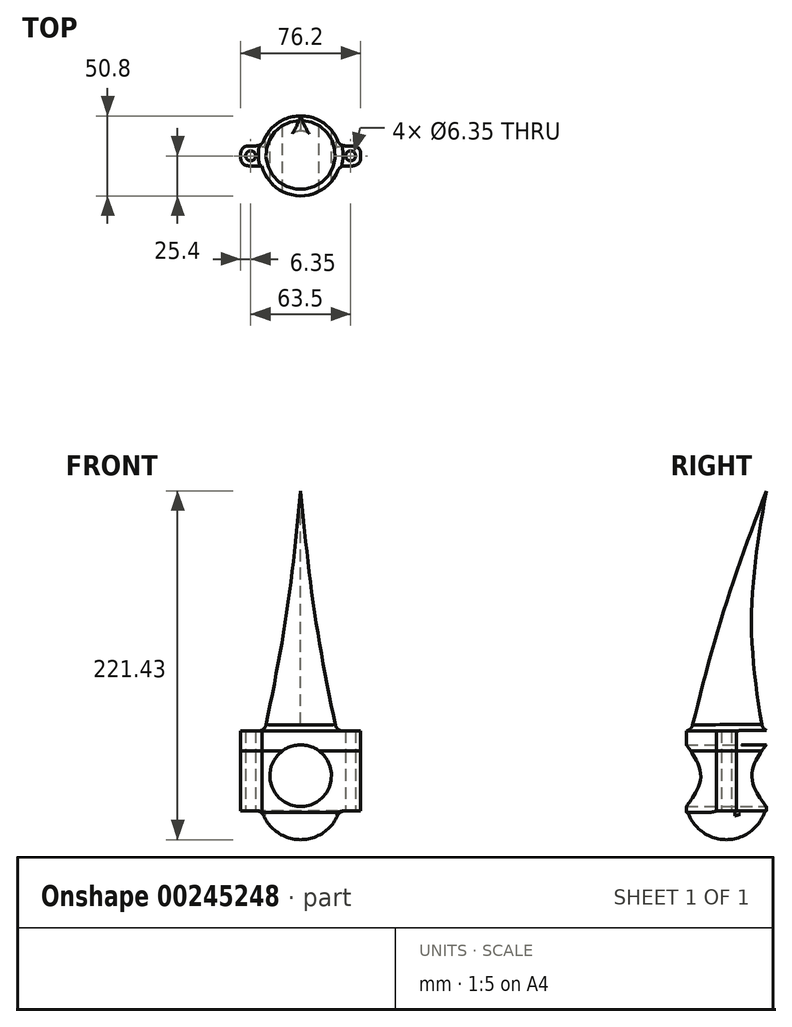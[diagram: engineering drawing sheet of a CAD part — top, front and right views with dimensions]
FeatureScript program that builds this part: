
annotation { "Feature Type Name" : "Feature", "Feature Type Description" : "" }
export const myFeature = defineFeature(function(context is Context, id is Id, definition is map)
    precondition{}
    {
        {
            var Q0;
            Q0=qCreatedBy(makeId("Right.planeOp"),FACE);
            var sketch = newSketch(context, id + "F0", { "sketchPlane" : qUnion([Q0])});
            skPoint(sketch, "E0", {"position": v(25.4, 165.1) * mm});
            skFitSpline(sketch, "E1", {"points": [v(0, 0) * mm, v(25.4, 165.1) * mm], "startDerivative": vector(11.53, 261.51) * mm, "endDerivative": vector(41.6, 123.81) * mm});
            skPoint(sketch, "E2", {"position": v(2.05, 36.75) * mm});
            skPoint(sketch, "E3", {"position": v(4.31, 63.88) * mm});
            skPoint(sketch, "E4", {"position": v(7.85, 92.76) * mm});
            skPoint(sketch, "E5", {"position": v(10.88, 110.73) * mm});
            skSolve(sketch);
        }
        {
            var Q0;
            Q0=qCreatedBy(makeId("Top.planeOp"),FACE);
            var sketch = newSketch(context, id + "F1", { "sketchPlane" : qUnion([Q0])});
            skCircle(sketch, "E6", {"center": v(0, 0) * mm, "radius": 25.4 * mm});
            skSolve(sketch);
        }
        {
            var Q0;
            Q0=sQuery(id+"F0.wireOp",EDGE,"E1");
            cPoint(context, id + "F2", {"entities" : qUnion([Q0]), "parameter" : 0.5});
        }
        {
            var Q0;
            Q0=sQuery(id+"F0.wireOp",EDGE,"E1");
            var Q1;
            Q1 = qCreatedBy(id + "F2" ,VERTEX);
            cPlane(context, id + "F3", {"entities" : qUnion([Q0, Q1]), "cplaneType" : CPlaneType.CURVE_POINT, "offset" : 25.4 * mm, "width" : 152.4 * mm, "height" : 152.4 * mm});
        }
        {
            var Q0;
            Q0=qCreatedBy(id+"F3.planeOp",FACE);
            var sketch = newSketch(context, id + "F4", { "sketchPlane" : qUnion([Q0])});
            skCircle(sketch, "E7", {"center": v(0, -4.31) * mm, "radius": 9.53 * mm});
            skSolve(sketch);
        }
        {
            var Q0;
            Q0=sQuery(id+"F0.wireOp",VERTEX,"E2");
            var Q1;
            Q1=sQuery(id+"F0.wireOp",EDGE,"E1");
            cPlane(context, id + "F5", {"entities" : qUnion([Q0, Q1]), "cplaneType" : CPlaneType.CURVE_POINT, "offset" : 25.4 * mm, "width" : 152.4 * mm, "height" : 152.4 * mm});
        }
        {
            var Q0;
            Q0=sQuery(id+"F0.wireOp",VERTEX,"E3");
            var Q1;
            Q1=sQuery(id+"F0.wireOp",EDGE,"E1");
            cPlane(context, id + "F6", {"entities" : qUnion([Q0, Q1]), "cplaneType" : CPlaneType.CURVE_POINT, "offset" : 25.4 * mm, "width" : 152.4 * mm, "height" : 152.4 * mm});
        }
        {
            var Q0;
            Q0=makeQuery(id+"F1.imprint","IMPRINT",FACE,{"disambiguationData":[TD([[makeQuery(id+"F1.imprint","IMPRINT",EDGE,{"derivedFrom":sQuery(id+"F1.wireOp",EDGE,"E6")}),1.0]])]});
            var Q1;
            Q1 = qSketchRegion(id + "F4", true);
            var Q2;
            Q2=sQuery(id+"F0.wireOp",VERTEX,"E0");
            loft(context, id + "F7", {"sheetProfilesArray" : [{ "sheetProfileEntities" : qUnion([Q0]) }, { "sheetProfileEntities" : qUnion([Q1]) }, { "sheetProfileEntities" : qUnion([Q2]) }]});
        }
        {
            var Q0;
            Q0=qCreatedBy(makeId("Top.planeOp"),FACE);
            var sketch = newSketch(context, id + "F8", { "sketchPlane" : qUnion([Q0])});
            skArc(sketch, "E8", {"start": v(24.6, 6.35) * mm, "mid": v(0, 25.4) * mm, "end": v(-24.6, 6.35) * mm});
            skLineSegment(sketch, "E9.bottom", {"start": v(-38.1, 6.35) * mm, "end": v(-24.6, 6.35) * mm});
            skLineSegment(sketch, "E9.top", {"start": v(-38.1, -6.35) * mm, "end": v(-24.6, -6.35) * mm});
            skLineSegment(sketch, "E9.left", {"start": v(-38.1, 6.35) * mm, "end": v(-38.1, -6.35) * mm});
            skLineSegment(sketch, "E9.right", {"start": v(38.1, 6.35) * mm, "end": v(38.1, -6.35) * mm});
            skLineSegment(sketch, "E10.trimOffspring", {"start": v(24.6, -6.35) * mm, "end": v(38.1, -6.35) * mm});
            skLineSegment(sketch, "E11.trimOffspring", {"start": v(24.6, 6.35) * mm, "end": v(38.1, 6.35) * mm});
            skArc(sketch, "E12.trimOffspring", {"start": v(-24.6, -6.35) * mm, "mid": v(0, -25.4) * mm, "end": v(24.6, -6.35) * mm});
            skPoint(sketch, "E13", {"position": v(-31.75, 0) * mm});
            skPoint(sketch, "E14", {"position": v(31.75, 0) * mm});
            skSolve(sketch);
        }
        {
            var Q0;
            Q0 = qSketchRegion(id + "F8", true);
            extrude(context, id + "F9", {"entities" : qUnion([Q0]), "operationType" : NewBodyOperationType.ADD, "depth" : 12.7 * mm});
        }
        {
            var Q0;
            Q0 = qSketchRegion(id + "F8", true);
            extrude(context, id + "F10", {"entities" : qUnion([Q0]), "oppositeDirection" : true, "depth" : 38.1 * mm});
        }
        {
            var Q0;
            Q0=qCreatedBy(makeId("Front.planeOp"),FACE);
            var sketch = newSketch(context, id + "F11", { "sketchPlane" : qUnion([Q0])});
            skCircle(sketch, "E15", {"center": v(0, -15.71) * mm, "radius": 19.57 * mm});
            skSolve(sketch);
        }
        {
            var Q0;
            Q0 = qSketchRegion(id + "F11", true);
            extrude(context, id + "F12", {"entities" : qUnion([Q0]), "operationType" : NewBodyOperationType.REMOVE, "depth" : 25.4 * mm, "hasSecondDirection" : true, "secondDirectionOppositeDirection" : true, "secondDirectionDepth" : 25.4 * mm});
        }
        {
            var Q0;
            Q0=makeQuery(id+"F9.boolean.opBoolean","INTERSECT",EDGE,{"derivedFrom":[makeQuery(id+"F7.opLoft","SWEPT_FACE",FACE,{"disambiguationData":[OSD([sQuery(id+"F0.wireOp",VERTEX,"E0"),sQuery(id+"F1.wireOp",EDGE,"E6"),sQuery(id+"F4.wireOp",EDGE,"E7")])]}),makeQuery(id+"F9.opExtrude","CAP_FACE",FACE,{"disambiguationData":[OSD([sQuery(id+"F8.wireOp",EDGE,"E8"),sQuery(id+"F8.wireOp",EDGE,"E9.bottom"),sQuery(id+"F8.wireOp",EDGE,"E9.top"),sQuery(id+"F8.wireOp",EDGE,"E9.left"),sQuery(id+"F8.wireOp",EDGE,"E9.right"),sQuery(id+"F8.wireOp",EDGE,"E10.trimOffspring"),sQuery(id+"F8.wireOp",EDGE,"E11.trimOffspring"),sQuery(id+"F8.wireOp",EDGE,"E12.trimOffspring")])],"isStart":false})]});
            fillet(context, id + "F13", {"entities" : qUnion([Q0]), "radius" : 5.08 * mm, "tangentPropagation" : true, "allowEdgeOverflow" : false});
        }
        {
            var Q0;
            Q0=qCreatedBy(makeId("Front.planeOp"),FACE);
            var sketch = newSketch(context, id + "F14", { "sketchPlane" : qUnion([Q0])});
            skArc(sketch, "E16", {"start": v(0, -56.33) * mm, "mid": v(15.32, -51.25) * mm, "end": v(24.6, -38.03) * mm});
            skLineSegment(sketch, "E17", {"start": v(24.6, -38.03) * mm, "end": v(0, -38.07) * mm});
            skLineSegment(sketch, "E18", {"start": v(0, -64.16) * mm, "end": v(0, -21.9) * mm, "construction": true});
            skLineSegment(sketch, "E19", {"start": v(0, -56.33) * mm, "end": v(0, -38.07) * mm});
            skSolve(sketch);
        }
        {
            var Q0;
            Q0 = qSketchRegion(id + "F14", true);
            var Q1;
            Q1=sQuery(id+"F14.wireOp",EDGE,"E18");
            revolve(context, id + "F15", {"operationType" : NewBodyOperationType.ADD, "entities" : qUnion([Q0]), "axis" : qUnion([Q1]), "revolveType" : RevolveType.FULL});
        }
        {
            var Q0;
            Q0=makeQuery(id+"F10.opExtrude","CAP_FACE",FACE,{"disambiguationData":[OSD([sQuery(id+"F8.wireOp",EDGE,"E8"),sQuery(id+"F8.wireOp",EDGE,"E9.bottom"),sQuery(id+"F8.wireOp",EDGE,"E9.top"),sQuery(id+"F8.wireOp",EDGE,"E9.left"),sQuery(id+"F8.wireOp",EDGE,"E9.right"),sQuery(id+"F8.wireOp",EDGE,"E10.trimOffspring"),sQuery(id+"F8.wireOp",EDGE,"E11.trimOffspring"),sQuery(id+"F8.wireOp",EDGE,"E12.trimOffspring")])],"isStart":false});
            var sketch = newSketch(context, id + "F16", { "sketchPlane" : qUnion([Q0])});
            skPoint(sketch, "E20", {"position": v(31.75, 0) * mm});
            skPoint(sketch, "E20.positionSnap0", {"position": v(38.1, 0) * mm});
            skPoint(sketch, "E21", {"position": v(-31.75, 0) * mm});
            skSolve(sketch);
        }
        {
            var Q0;
            Q0=sQuery(id+"F16.wireOp",VERTEX,"E20");
            var Q1;
            Q1=sQuery(id+"F16.wireOp",VERTEX,"E21");
            var Q2;
            Q2=makeQuery(id+"F7.opLoft","SWEPT_BODY",BODY,{"disambiguationData":[OSD([sQuery(id+"F0.wireOp",VERTEX,"E0"),makeQuery(id+"F1.imprint","IMPRINT",FACE,{"disambiguationData":[TD([[makeQuery(id+"F1.imprint","IMPRINT",EDGE,{"derivedFrom":sQuery(id+"F1.wireOp",EDGE,"E6")}),1.0]])]}),sQuery(id+"F4.wireOp",EDGE,"E7")])]});
            var Q3;
            Q3=makeQuery(id+"F10.opExtrude","SWEPT_BODY",BODY,{"disambiguationData":[OSD([sQuery(id+"F8.wireOp",EDGE,"E8"),sQuery(id+"F8.wireOp",EDGE,"E9.bottom"),sQuery(id+"F8.wireOp",EDGE,"E9.top"),sQuery(id+"F8.wireOp",EDGE,"E9.left"),sQuery(id+"F8.wireOp",EDGE,"E9.right"),sQuery(id+"F8.wireOp",EDGE,"E10.trimOffspring"),sQuery(id+"F8.wireOp",EDGE,"E11.trimOffspring"),sQuery(id+"F8.wireOp",EDGE,"E12.trimOffspring")])]});
            hole(context, id + "F17", {"style" : HoleStyle.SIMPLE, "endStyle" : HoleEndStyle.THROUGH, "holeDiameter" : 6.35 * mm, "tappedDepth" : 12.7 * mm, "tapClearance" : 3, "locations" : qUnion([Q0, Q1]), "scope" : qUnion([Q2, Q3])});
        }
        {
            var Q0;
            Q0=makeQuery(id+"F10.opExtrude","SWEPT_EDGE",EDGE,{"disambiguationData":[OSD([sQuery(id+"F8.wireOp",EDGE,"E10.trimOffspring"),sQuery(id+"F8.wireOp",EDGE,"E12.trimOffspring")])]});
            var Q1;
            Q1=makeQuery(id+"F9.opExtrude","SWEPT_EDGE",EDGE,{"disambiguationData":[OSD([sQuery(id+"F8.wireOp",EDGE,"E10.trimOffspring"),sQuery(id+"F8.wireOp",EDGE,"E12.trimOffspring")])]});
            fillet(context, id + "F18", {"entities" : qUnion([Q0, Q1]), "radius" : 5.08 * mm, "tangentPropagation" : true, "allowEdgeOverflow" : false});
        }
        {
            var Q0;
            Q0=makeQuery(id+"F10.opExtrude","SWEPT_EDGE",EDGE,{"disambiguationData":[OSD([sQuery(id+"F8.wireOp",EDGE,"E9.right"),sQuery(id+"F8.wireOp",EDGE,"E10.trimOffspring")])]});
            var Q1;
            Q1=makeQuery(id+"F9.opExtrude","SWEPT_EDGE",EDGE,{"disambiguationData":[OSD([sQuery(id+"F8.wireOp",EDGE,"E9.right"),sQuery(id+"F8.wireOp",EDGE,"E10.trimOffspring")])]});
            var Q2;
            Q2=makeQuery(id+"F9.opExtrude","SWEPT_EDGE",EDGE,{"disambiguationData":[OSD([sQuery(id+"F8.wireOp",EDGE,"E9.right"),sQuery(id+"F8.wireOp",EDGE,"E11.trimOffspring")])]});
            var Q3;
            Q3=makeQuery(id+"F10.opExtrude","SWEPT_EDGE",EDGE,{"disambiguationData":[OSD([sQuery(id+"F8.wireOp",EDGE,"E9.right"),sQuery(id+"F8.wireOp",EDGE,"E11.trimOffspring")])]});
            var Q4;
            Q4=makeQuery(id+"F9.opExtrude","SWEPT_EDGE",EDGE,{"disambiguationData":[OSD([sQuery(id+"F8.wireOp",EDGE,"E9.top"),sQuery(id+"F8.wireOp",EDGE,"E9.left")])]});
            var Q5;
            Q5=makeQuery(id+"F10.opExtrude","SWEPT_EDGE",EDGE,{"disambiguationData":[OSD([sQuery(id+"F8.wireOp",EDGE,"E9.top"),sQuery(id+"F8.wireOp",EDGE,"E9.left")])]});
            var Q6;
            Q6=makeQuery(id+"F9.opExtrude","SWEPT_EDGE",EDGE,{"disambiguationData":[OSD([sQuery(id+"F8.wireOp",EDGE,"E9.bottom"),sQuery(id+"F8.wireOp",EDGE,"E9.left")])]});
            var Q7;
            Q7=makeQuery(id+"F10.opExtrude","SWEPT_EDGE",EDGE,{"disambiguationData":[OSD([sQuery(id+"F8.wireOp",EDGE,"E9.bottom"),sQuery(id+"F8.wireOp",EDGE,"E9.left")])]});
            fillet(context, id + "F19", {"entities" : qUnion([Q0, Q1, Q2, Q3, Q4, Q5, Q6, Q7]), "radius" : 5.08 * mm, "tangentPropagation" : true, "allowEdgeOverflow" : false});
        }
        {
            var Q0;
            Q0=makeQuery(id+"F10.opExtrude","SWEPT_EDGE",EDGE,{"disambiguationData":[OSD([sQuery(id+"F8.wireOp",EDGE,"E8"),sQuery(id+"F8.wireOp",EDGE,"E9.bottom")])]});
            var Q1;
            Q1=makeQuery(id+"F9.opExtrude","SWEPT_EDGE",EDGE,{"disambiguationData":[OSD([sQuery(id+"F8.wireOp",EDGE,"E8"),sQuery(id+"F8.wireOp",EDGE,"E9.bottom")])]});
            var Q2;
            Q2=makeQuery(id+"F10.opExtrude","SWEPT_EDGE",EDGE,{"disambiguationData":[OSD([sQuery(id+"F8.wireOp",EDGE,"E8"),sQuery(id+"F8.wireOp",EDGE,"E11.trimOffspring")])]});
            var Q3;
            Q3=makeQuery(id+"F9.opExtrude","SWEPT_EDGE",EDGE,{"disambiguationData":[OSD([sQuery(id+"F8.wireOp",EDGE,"E8"),sQuery(id+"F8.wireOp",EDGE,"E11.trimOffspring")])]});
            fillet(context, id + "F20", {"entities" : qUnion([Q0, Q1, Q2, Q3]), "radius" : 5.08 * mm, "tangentPropagation" : true, "allowEdgeOverflow" : false});
        }
        {
            var Q0;
            Q0=makeQuery(id+"F15.boolean.opBoolean","INTERSECT",EDGE,{"derivedFrom":[makeQuery(id+"F10.opExtrude","CAP_FACE",FACE,{"disambiguationData":[OSD([sQuery(id+"F8.wireOp",EDGE,"E8"),sQuery(id+"F8.wireOp",EDGE,"E9.bottom"),sQuery(id+"F8.wireOp",EDGE,"E9.top"),sQuery(id+"F8.wireOp",EDGE,"E9.left"),sQuery(id+"F8.wireOp",EDGE,"E9.right"),sQuery(id+"F8.wireOp",EDGE,"E10.trimOffspring"),sQuery(id+"F8.wireOp",EDGE,"E11.trimOffspring"),sQuery(id+"F8.wireOp",EDGE,"E12.trimOffspring")])],"isStart":false}),makeQuery(id+"F15.opRevolve","SWEPT_FACE",FACE,{"disambiguationData":[OSD([sQuery(id+"F14.wireOp",EDGE,"E16")])]})]});
            fillet(context, id + "F21", {"entities" : qUnion([Q0]), "radius" : 5.08 * mm, "tangentPropagation" : true, "allowEdgeOverflow" : false});
        }
        {
            var Q0;
            Q0=makeQuery(id+"F7.opLoft","SWEPT_BODY",BODY,{"disambiguationData":[OSD([sQuery(id+"F0.wireOp",VERTEX,"E0"),makeQuery(id+"F1.imprint","IMPRINT",FACE,{"disambiguationData":[TD([[makeQuery(id+"F1.imprint","IMPRINT",EDGE,{"derivedFrom":sQuery(id+"F1.wireOp",EDGE,"E6")}),1.0]])]}),sQuery(id+"F4.wireOp",EDGE,"E7")])]});
            transform(context, id + "F22", {"entities" : qUnion([Q0]), "transformType" : TransformType.TRANSLATION_3D, "dx" : 0 * mm, "dy" : 0 * mm, "dz" : 0 * mm, "makeCopy" : true});
        }
        {
            var Q0;
            Q0=makeQuery(id+"F22.opPattern","COPY",BODY,{"derivedFrom":makeQuery(id+"F7.opLoft","SWEPT_BODY",BODY,{"disambiguationData":[OSD([sQuery(id+"F0.wireOp",VERTEX,"E0"),makeQuery(id+"F1.imprint","IMPRINT",FACE,{"disambiguationData":[TD([[makeQuery(id+"F1.imprint","IMPRINT",EDGE,{"derivedFrom":sQuery(id+"F1.wireOp",EDGE,"E6")}),1.0]])]}),sQuery(id+"F4.wireOp",EDGE,"E7")])]}),"instanceName":"1"});
            deleteBodies(context, id + "F23", {"entities" : qUnion([Q0])});
        }
        {
            var Q0;
            Q0=makeQuery(id+"F7.opLoft","SWEPT_BODY",BODY,{"disambiguationData":[OSD([sQuery(id+"F0.wireOp",VERTEX,"E0"),makeQuery(id+"F1.imprint","IMPRINT",FACE,{"disambiguationData":[TD([[makeQuery(id+"F1.imprint","IMPRINT",EDGE,{"derivedFrom":sQuery(id+"F1.wireOp",EDGE,"E6")}),1.0]])]}),sQuery(id+"F4.wireOp",EDGE,"E7")])]});
            transform(context, id + "F24", {"entities" : qUnion([Q0]), "transformType" : TransformType.TRANSLATION_3D, "dx" : 254 * mm, "dy" : 0 * mm, "dz" : 0 * mm, "makeCopy" : true});
        }
        {
            var Q0;
            Q0=makeQuery(id+"F24.opPattern","COPY",BODY,{"derivedFrom":makeQuery(id+"F7.opLoft","SWEPT_BODY",BODY,{"disambiguationData":[OSD([sQuery(id+"F0.wireOp",VERTEX,"E0"),makeQuery(id+"F1.imprint","IMPRINT",FACE,{"disambiguationData":[TD([[makeQuery(id+"F1.imprint","IMPRINT",EDGE,{"derivedFrom":sQuery(id+"F1.wireOp",EDGE,"E6")}),1.0]])]}),sQuery(id+"F4.wireOp",EDGE,"E7")])]}),"instanceName":"1"});
            deleteBodies(context, id + "F25", {"entities" : qUnion([Q0])});
        }
    });
